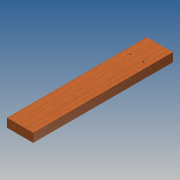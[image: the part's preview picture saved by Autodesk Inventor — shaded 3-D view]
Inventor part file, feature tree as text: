
AUTODESK INVENTOR PART (.ipt)
format: ipt  version: 2014 SP1 (Build 180222100, 222)  size: 100,352 bytes
history: native  units: in
note: dims shown in document units (in); Inventor stores cm internally (conversion verified against a paired STEP export)
features: sketch x3, hole x2, extrude x1
ambient origin geometry x8: Origin, YZ Plane, XZ Plane, XY Plane, X Axis, Y Axis, Z Axis, Center Point
bodies: Solid1 (feature_tree)
feature tree (6):
  extrude  "Extrusion1"  Depth=1.4961in
  hole  "Hole1"  [1 undecoded]
  hole  "Hole2"  [1 undecoded]
  sketch  "Sketch1"  dims[d0=4.4882in d1=1.4961in]
  sketch  "Sketch2"  dims[d2=24.0in d3=0.0in d5=0.7874in d7=2.2441in d8=0.3937in d10=1.0in]
  sketch  "Sketch3"  dims[d12=0.25in d13=0.75in d14=0.375in d15=0.25in d16=0.5635in d17=1.0in d18=0.8108in d21=0.7874in d23=2.2441in d24=0.3937in d26=1.0in d28=0.25in d29=0.75in d30=0.375in d31=0.25in d32=0.5635in d33=1.0in d34=0.8108in d36=3.937in]
note: 2 required parameter values undecoded (feature->parameter linkage not recoverable at this tier; creation-order binding heuristic only, values carry confidence <= 0.55)
